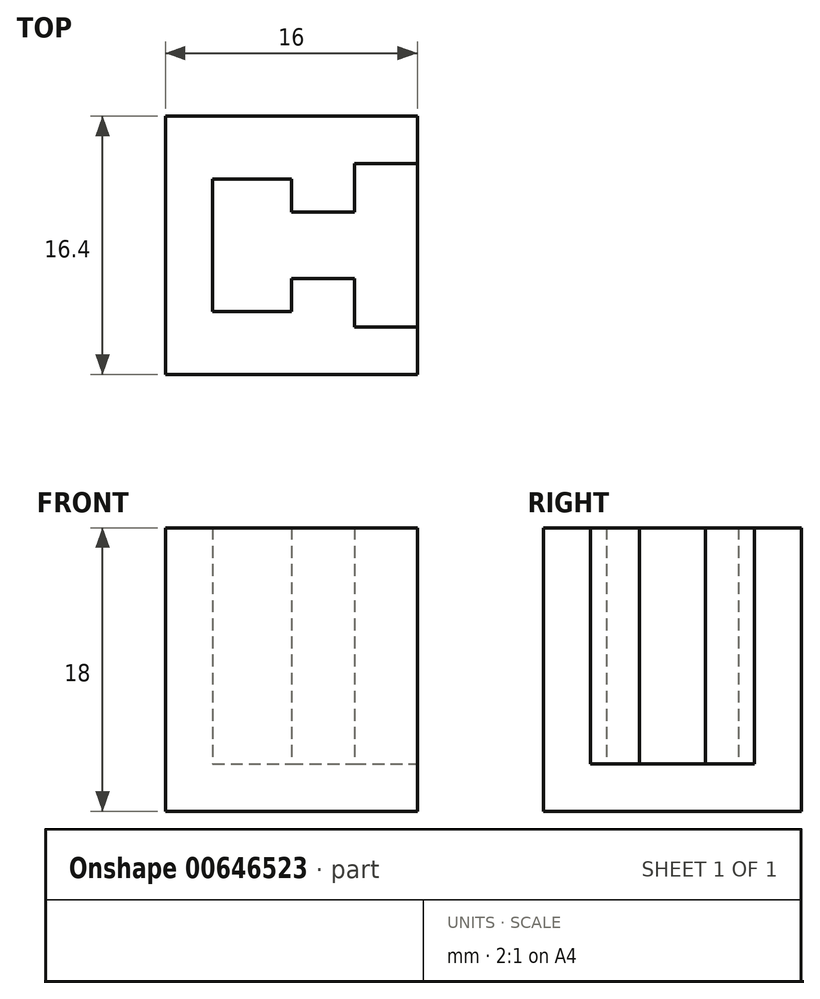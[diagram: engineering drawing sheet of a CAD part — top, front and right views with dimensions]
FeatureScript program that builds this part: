
annotation { "Feature Type Name" : "Feature", "Feature Type Description" : "" }
export const myFeature = defineFeature(function(context is Context, id is Id, definition is map)
    precondition{}
    {
        {
            var Q0;
            Q0=qCreatedBy(makeId("Top.planeOp"),FACE);
            var sketch = newSketch(context, id + "F0", { "sketchPlane" : qUnion([Q0])});
            skLineSegment(sketch, "E0", {"start": v(0, 0) * mm, "end": v(5, 0) * mm});
            skLineSegment(sketch, "E1", {"start": v(5, 0) * mm, "end": v(5, -2.1) * mm});
            skLineSegment(sketch, "E2", {"start": v(5, -2.1) * mm, "end": v(9, -2.1) * mm});
            skLineSegment(sketch, "E3", {"start": v(9, -2.1) * mm, "end": v(9, 1) * mm});
            skLineSegment(sketch, "E4", {"start": v(9, 1) * mm, "end": v(13, 1) * mm});
            skLineSegment(sketch, "E5", {"start": v(13, 1) * mm, "end": v(13, 4) * mm});
            skLineSegment(sketch, "E6", {"start": v(13, 4) * mm, "end": v(-3, 4) * mm});
            skLineSegment(sketch, "E7", {"start": v(-3, 4) * mm, "end": v(-3, -12.4) * mm});
            skLineSegment(sketch, "E8", {"start": v(-3, -12.4) * mm, "end": v(13, -12.4) * mm});
            skLineSegment(sketch, "E9", {"start": v(13, -12.4) * mm, "end": v(13, -9.4) * mm});
            skLineSegment(sketch, "E10", {"start": v(13, -9.4) * mm, "end": v(9, -9.4) * mm});
            skLineSegment(sketch, "E11", {"start": v(9, -9.4) * mm, "end": v(9, -6.3) * mm});
            skLineSegment(sketch, "E12", {"start": v(9, -6.3) * mm, "end": v(5, -6.3) * mm});
            skLineSegment(sketch, "E13", {"start": v(5, -6.3) * mm, "end": v(5, -8.4) * mm});
            skLineSegment(sketch, "E14", {"start": v(5, -8.4) * mm, "end": v(0, -8.4) * mm});
            skLineSegment(sketch, "E15", {"start": v(0, -8.4) * mm, "end": v(0, 0) * mm});
            skLineSegment(sketch, "E16", {"start": v(0, 0) * mm, "end": v(-3, 0) * mm});
            skLineSegment(sketch, "E17", {"start": v(0, -8.4) * mm, "end": v(-3, -8.4) * mm});
            skLineSegment(sketch, "E18", {"start": v(13, -9.4) * mm, "end": v(13, 1) * mm});
            skSolve(sketch);
        }
        {
            var Q0;
            Q0=makeQuery(id+"F0.imprint","IMPRINT",FACE,{"disambiguationData":[TD([[makeQuery(id+"F0.imprint","IMPRINT",EDGE,{"derivedFrom":sQuery(id+"F0.wireOp",EDGE,"E0")}),1.0]])]});
            var Q1;
            Q1=makeQuery(id+"F0.imprint","IMPRINT",FACE,{"disambiguationData":[TD([[makeQuery(id+"F0.imprint","IMPRINT",EDGE,{"derivedFrom":sQuery(id+"F0.wireOp",EDGE,"E15")}),1.0]])]});
            var Q2;
            {var subQ0=sQuery(id+"F0.wireOp",EDGE,"E8");Q2=makeQuery(id+"F0.imprint","IMPRINT",FACE,{"disambiguationData":[TD([[makeQuery(id+"F0.imprint","IMPRINT",EDGE,{"derivedFrom":subQ0}),1.0]])]});}
            var Q3;
            Q3=makeQuery(id+"F0.imprint","IMPRINT",FACE,{"disambiguationData":[TD([[makeQuery(id+"F0.imprint","IMPRINT",EDGE,{"derivedFrom":sQuery(id+"F0.wireOp",EDGE,"E0")}),-1.0]])]});
            extrude(context, id + "F1", {"entities" : qUnion([Q0, Q1, Q2, Q3]), "oppositeDirection" : true, "depth" : 3 * mm, "offsetDistance" : 25 * mm});
        }
        {
            var Q0;
            Q0=makeQuery(id+"F0.imprint","IMPRINT",FACE,{"disambiguationData":[TD([[makeQuery(id+"F0.imprint","IMPRINT",EDGE,{"derivedFrom":sQuery(id+"F0.wireOp",EDGE,"E0")}),1.0]])]});
            var Q1;
            {var subQ0=sQuery(id+"F0.wireOp",EDGE,"E8");Q1=makeQuery(id+"F0.imprint","IMPRINT",FACE,{"disambiguationData":[TD([[makeQuery(id+"F0.imprint","IMPRINT",EDGE,{"derivedFrom":subQ0}),1.0]])]});}
            var Q2;
            Q2=makeQuery(id+"F0.imprint","IMPRINT",FACE,{"disambiguationData":[TD([[makeQuery(id+"F0.imprint","IMPRINT",EDGE,{"derivedFrom":sQuery(id+"F0.wireOp",EDGE,"E15")}),1.0]])]});
            extrude(context, id + "F2", {"entities" : qUnion([Q0, Q1, Q2]), "operationType" : NewBodyOperationType.ADD, "depth" : 15 * mm, "offsetDistance" : 25 * mm});
        }
    });
